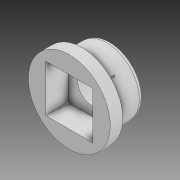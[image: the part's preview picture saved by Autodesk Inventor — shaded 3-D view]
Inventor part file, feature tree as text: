
AUTODESK INVENTOR PART (.ipt)
format: ipt  version: 2020 (Build 240168000, 168)  size: 140,288 bytes
history: native  units: mm
features: sketch x2, revolve x1, extrude x1, fillet x1
ambient origin geometry x8: Origin, YZ Plane, XZ Plane, XY Plane, X Axis, Y Axis, Z Axis, Center Point
bodies: Solid1 (feature_tree)
feature tree (5):
  revolve  "Revolution1"  [1 undecoded]
  extrude  "Extrusion1"  Depth=1.5mm
  fillet  "Fillet1"  Radius=3.5mm
  sketch  "Sketch1"  dims[d0=1.7mm d1=3.95mm]
  sketch  "Sketch2"  dims[d2=1.0mm d3=1.5mm d4=3.5mm d5=90.0deg d6=5.7mm d7=2.7mm d8=0.0mm d9=0.5mm]
note: 1 required parameter value undecoded (feature->parameter linkage not recoverable at this tier; creation-order binding heuristic only, values carry confidence <= 0.55)
